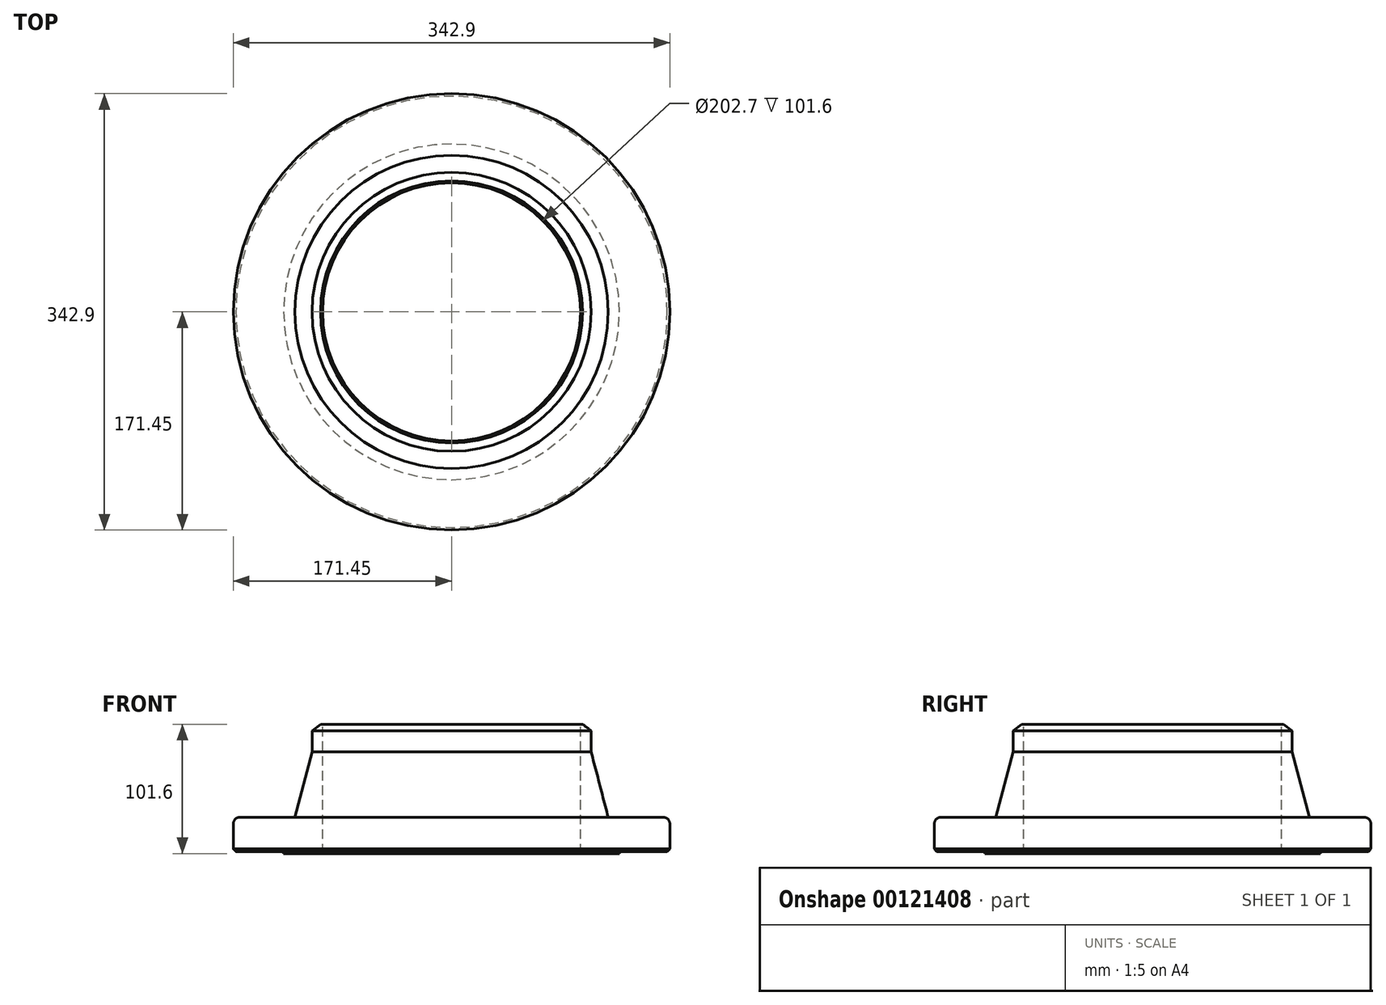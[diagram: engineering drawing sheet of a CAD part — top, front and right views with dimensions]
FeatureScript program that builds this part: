
annotation { "Feature Type Name" : "Feature", "Feature Type Description" : "" }
export const myFeature = defineFeature(function(context is Context, id is Id, definition is map)
    precondition{}
    {
        {
            var Q0;
            Q0=qCreatedBy(makeId("Front.planeOp"),FACE);
            var sketch = newSketch(context, id + "F0", { "sketchPlane" : qUnion([Q0])});
            skLineSegment(sketch, "E0", {"start": v(-79.45, 89.03) * mm, "end": v(-81.05, 89.03) * mm});
            skLineSegment(sketch, "E1", {"start": v(-101.15, 15.83) * mm, "end": v(-149.55, 15.83) * mm});
            skLineSegment(sketch, "E2", {"start": v(-149.55, 15.83) * mm, "end": v(-149.55, -10.97) * mm});
            skLineSegment(sketch, "E3", {"start": v(21.9, 156.74) * mm, "end": v(21.9, -154.82) * mm});
            skLineSegment(sketch, "E4", {"start": v(-79.45, -12.57) * mm, "end": v(-79.45, 89.03) * mm});
            skLineSegment(sketch, "E5", {"start": v(-79.45, -12.57) * mm, "end": v(-109.95, -12.57) * mm});
            skLineSegment(sketch, "E6", {"start": v(-149.55, -10.97) * mm, "end": v(-109.95, -10.97) * mm});
            skLineSegment(sketch, "E7", {"start": v(-109.95, -10.97) * mm, "end": v(-109.95, -12.57) * mm});
            skLineSegment(sketch, "E8", {"start": v(-87.7, 83.93) * mm, "end": v(-81.05, 89.03) * mm});
            skLineSegment(sketch, "E9", {"start": v(-87.7, 83.93) * mm, "end": v(-87.7, 67.37) * mm});
            skLineSegment(sketch, "E10", {"start": v(-87.7, 67.37) * mm, "end": v(-101.15, 15.83) * mm});
            skSolve(sketch);
        }
        {
            var Q0;
            Q0=makeQuery(id+"F0.imprint","IMPRINT",FACE,{"disambiguationData":[TD([[makeQuery(id+"F0.imprint","IMPRINT",EDGE,{"derivedFrom":sQuery(id+"F0.wireOp",EDGE,"E0")}),1.0]])]});
            var Q1;
            Q1=sQuery(id+"F0.wireOp",EDGE,"E3");
            revolve(context, id + "F1", {"entities" : qUnion([Q0]), "axis" : qUnion([Q1]), "revolveType" : RevolveType.FULL});
        }
        {
            var Q0;
            Q0=makeQuery(id+"F1.opRevolve","SWEPT_EDGE",EDGE,{"disambiguationData":[OSD([sQuery(id+"F0.wireOp",EDGE,"E1"),sQuery(id+"F0.wireOp",EDGE,"E2")])]});
            fillet(context, id + "F2", {"entities" : qUnion([Q0]), "radius" : 5 * mm, "tangentPropagation" : true, "allowEdgeOverflow" : false});
        }
        {
            var Q0;
            Q0=makeQuery(id+"F1.opRevolve","SWEPT_EDGE",EDGE,{"disambiguationData":[OSD([sQuery(id+"F0.wireOp",EDGE,"E2"),sQuery(id+"F0.wireOp",EDGE,"E6")])]});
            chamfer(context, id + "F3", {"entities" : qUnion([Q0]), "width" : 2 * mm, "tangentPropagation" : true});
        }
    });
